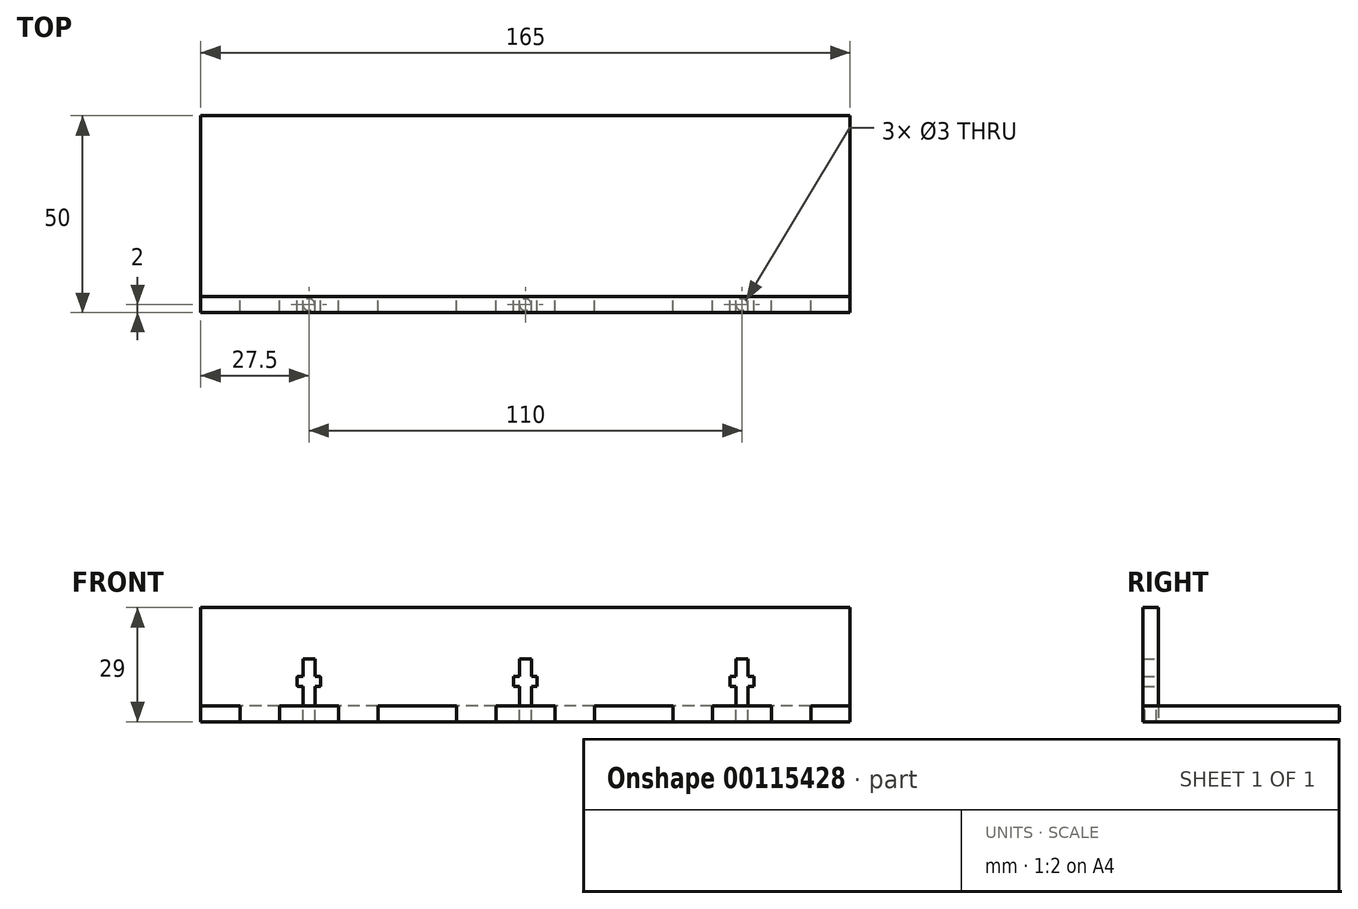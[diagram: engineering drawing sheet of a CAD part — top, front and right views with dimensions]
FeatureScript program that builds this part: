
annotation { "Feature Type Name" : "Feature", "Feature Type Description" : "" }
export const myFeature = defineFeature(function(context is Context, id is Id, definition is map)
    precondition{}
    {
        {
            var Q0;
            Q0=qCreatedBy(makeId("Front.planeOp"),FACE);
            var sketch = newSketch(context, id + "F0", { "sketchPlane" : qUnion([Q0])});
            skLineSegment(sketch, "E0.top", {"start": v(-2.5, 25) * mm, "end": v(162.5, 25) * mm});
            skLineSegment(sketch, "E0.left", {"start": v(-2.5, 0) * mm, "end": v(-2.5, 25) * mm});
            skLineSegment(sketch, "E0.right", {"start": v(162.5, 0) * mm, "end": v(162.5, 25) * mm});
            skLineSegment(sketch, "E1.trimOffspring", {"start": v(-2.5, 0) * mm, "end": v(7.5, 0) * mm});
            skLineSegment(sketch, "E2.top", {"start": v(23.5, 12) * mm, "end": v(26.5, 12) * mm});
            skLineSegment(sketch, "E2.left", {"start": v(23.5, 0) * mm, "end": v(23.5, 5) * mm});
            skLineSegment(sketch, "E2.right", {"start": v(26.5, 0) * mm, "end": v(26.5, 5) * mm});
            skLineSegment(sketch, "E3", {"start": v(25, 12) * mm, "end": v(25, 0) * mm, "construction": true});
            skLineSegment(sketch, "E4.bottom", {"start": v(27.75, 5) * mm, "end": v(26.5, 5) * mm});
            skLineSegment(sketch, "E4.top", {"start": v(27.75, 7.5) * mm, "end": v(26.5, 7.5) * mm});
            skLineSegment(sketch, "E4.left", {"start": v(28, 5.25) * mm, "end": v(28, 7.25) * mm});
            skLineSegment(sketch, "E4.right", {"start": v(22, 5.25) * mm, "end": v(22, 7.25) * mm});
            skPoint(sketch, "E4.middle", {"position": v(25, 6.25) * mm});
            skLineSegment(sketch, "E5.top", {"start": v(32.5, -4) * mm, "end": v(42.5, -4) * mm});
            skLineSegment(sketch, "E5.left", {"start": v(32.5, 0) * mm, "end": v(32.5, -4) * mm});
            skLineSegment(sketch, "E5.right", {"start": v(42.5, 0) * mm, "end": v(42.5, -4) * mm});
            skLineSegment(sketch, "E6.top", {"start": v(7.5, -4) * mm, "end": v(17.5, -4) * mm});
            skLineSegment(sketch, "E6.left", {"start": v(7.5, 0) * mm, "end": v(7.5, -4) * mm});
            skLineSegment(sketch, "E6.right", {"start": v(17.5, 0) * mm, "end": v(17.5, -4) * mm});
            skLineSegment(sketch, "E7.trimOffspring", {"start": v(23.5, 7.5) * mm, "end": v(22.25, 7.5) * mm});
            skLineSegment(sketch, "E8.trimOffspring", {"start": v(26.5, 7.5) * mm, "end": v(26.5, 12) * mm});
            skLineSegment(sketch, "E9.trimOffspring", {"start": v(23.5, 5) * mm, "end": v(22.25, 5) * mm});
            skLineSegment(sketch, "E10.trimOffspring", {"start": v(23.5, 7.5) * mm, "end": v(23.5, 12) * mm});
            skLineSegment(sketch, "E11.trimOffspring", {"start": v(26.5, 0) * mm, "end": v(32.5, 0) * mm});
            skLineSegment(sketch, "E12.trimOffspring", {"start": v(42.5, 0) * mm, "end": v(62.5, 0) * mm});
            skLineSegment(sketch, "E13.trimOffspring", {"start": v(17.5, 0) * mm, "end": v(23.5, 0) * mm});
            skLineSegment(sketch, "E14.1.0.0", {"start": v(78.5, 0) * mm, "end": v(78.5, 5) * mm});
            skPoint(sketch, "E14.1.0.1", {"position": v(80, 6.25) * mm});
            skLineSegment(sketch, "E14.1.0.2", {"start": v(80, 12) * mm, "end": v(80, 0) * mm, "construction": true});
            skLineSegment(sketch, "E14.1.0.3", {"start": v(78.5, 7.5) * mm, "end": v(78.5, 12) * mm});
            skLineSegment(sketch, "E14.1.0.4", {"start": v(81.5, 7.5) * mm, "end": v(81.5, 12) * mm});
            skLineSegment(sketch, "E14.1.0.5", {"start": v(81.5, 0) * mm, "end": v(81.5, 5) * mm});
            skLineSegment(sketch, "E14.1.0.6", {"start": v(78.5, 5) * mm, "end": v(77, 5) * mm});
            skLineSegment(sketch, "E14.1.0.7", {"start": v(78.5, 7.5) * mm, "end": v(77, 7.5) * mm});
            skLineSegment(sketch, "E14.1.0.8", {"start": v(83, 7.5) * mm, "end": v(81.5, 7.5) * mm});
            skLineSegment(sketch, "E14.1.0.9", {"start": v(78.5, 12) * mm, "end": v(81.5, 12) * mm});
            skLineSegment(sketch, "E14.1.0.10", {"start": v(83, 5) * mm, "end": v(81.5, 5) * mm});
            skLineSegment(sketch, "E14.1.0.11", {"start": v(77, 5) * mm, "end": v(77, 7.5) * mm});
            skLineSegment(sketch, "E14.1.0.12", {"start": v(83, 5) * mm, "end": v(83, 7.5) * mm});
            skLineSegment(sketch, "E14.1.0.13", {"start": v(87.5, -4) * mm, "end": v(97.5, -4) * mm});
            skLineSegment(sketch, "E14.1.0.14", {"start": v(62.5, -4) * mm, "end": v(72.5, -4) * mm});
            skLineSegment(sketch, "E14.1.0.15", {"start": v(72.5, 0) * mm, "end": v(72.5, -4) * mm});
            skLineSegment(sketch, "E14.1.0.16", {"start": v(62.5, 0) * mm, "end": v(62.5, -4) * mm});
            skLineSegment(sketch, "E14.1.0.17", {"start": v(87.5, 0) * mm, "end": v(87.5, -4) * mm});
            skLineSegment(sketch, "E14.1.0.18", {"start": v(97.5, 0) * mm, "end": v(97.5, -4) * mm});
            skLineSegment(sketch, "E14.2.0.0", {"start": v(133.5, 0) * mm, "end": v(133.5, 5) * mm});
            skPoint(sketch, "E14.2.0.1", {"position": v(135, 6.25) * mm});
            skLineSegment(sketch, "E14.2.0.2", {"start": v(135, 12) * mm, "end": v(135, 0) * mm, "construction": true});
            skLineSegment(sketch, "E14.2.0.3", {"start": v(133.5, 7.5) * mm, "end": v(133.5, 12) * mm});
            skLineSegment(sketch, "E14.2.0.4", {"start": v(136.5, 7.5) * mm, "end": v(136.5, 12) * mm});
            skLineSegment(sketch, "E14.2.0.5", {"start": v(136.5, 0) * mm, "end": v(136.5, 5) * mm});
            skLineSegment(sketch, "E14.2.0.6", {"start": v(133.5, 5) * mm, "end": v(132, 5) * mm});
            skLineSegment(sketch, "E14.2.0.7", {"start": v(133.5, 7.5) * mm, "end": v(132, 7.5) * mm});
            skLineSegment(sketch, "E14.2.0.8", {"start": v(138, 7.5) * mm, "end": v(136.5, 7.5) * mm});
            skLineSegment(sketch, "E14.2.0.9", {"start": v(133.5, 12) * mm, "end": v(136.5, 12) * mm});
            skLineSegment(sketch, "E14.2.0.10", {"start": v(138, 5) * mm, "end": v(136.5, 5) * mm});
            skLineSegment(sketch, "E14.2.0.11", {"start": v(132, 5) * mm, "end": v(132, 7.5) * mm});
            skLineSegment(sketch, "E14.2.0.12", {"start": v(138, 5) * mm, "end": v(138, 7.5) * mm});
            skLineSegment(sketch, "E14.2.0.13", {"start": v(142.5, -4) * mm, "end": v(152.5, -4) * mm});
            skLineSegment(sketch, "E14.2.0.14", {"start": v(117.5, -4) * mm, "end": v(127.5, -4) * mm});
            skLineSegment(sketch, "E14.2.0.15", {"start": v(127.5, 0) * mm, "end": v(127.5, -4) * mm});
            skLineSegment(sketch, "E14.2.0.16", {"start": v(117.5, 0) * mm, "end": v(117.5, -4) * mm});
            skLineSegment(sketch, "E14.2.0.17", {"start": v(142.5, 0) * mm, "end": v(142.5, -4) * mm});
            skLineSegment(sketch, "E14.2.0.18", {"start": v(152.5, 0) * mm, "end": v(152.5, -4) * mm});
            skLineSegment(sketch, "E14.direction1", {"start": v(7.5, -4) * mm, "end": v(62.5, -4) * mm, "construction": true});
            skLineSegment(sketch, "E15.trimOffspring", {"start": v(152.5, 0) * mm, "end": v(162.5, 0) * mm});
            skLineSegment(sketch, "E16.trimOffspring", {"start": v(136.5, 0) * mm, "end": v(142.5, 0) * mm});
            skLineSegment(sketch, "E17.trimOffspring", {"start": v(127.5, 0) * mm, "end": v(133.5, 0) * mm});
            skLineSegment(sketch, "E18.trimOffspring", {"start": v(97.5, 0) * mm, "end": v(117.5, 0) * mm});
            skLineSegment(sketch, "E19.trimOffspring", {"start": v(81.5, 0) * mm, "end": v(87.5, 0) * mm});
            skLineSegment(sketch, "E20.trimOffspring", {"start": v(72.5, 0) * mm, "end": v(78.5, 0) * mm});
            skPoint(sketch, "E21.visualSharp", {"position": v(28, 5) * mm});
            skArc(sketch, "E21.filletArc", {"start": v(27.75, 5) * mm, "mid": v(27.93, 5.07) * mm, "end": v(28, 5.25) * mm});
            skPoint(sketch, "E22.visualSharp", {"position": v(28, 7.5) * mm});
            skArc(sketch, "E22.filletArc", {"start": v(28, 7.25) * mm, "mid": v(27.93, 7.43) * mm, "end": v(27.75, 7.5) * mm});
            skPoint(sketch, "E23.visualSharp", {"position": v(22, 5) * mm});
            skArc(sketch, "E23.filletArc", {"start": v(22, 5.25) * mm, "mid": v(22.07, 5.07) * mm, "end": v(22.25, 5) * mm});
            skPoint(sketch, "E24.visualSharp", {"position": v(22, 7.5) * mm});
            skArc(sketch, "E24.filletArc", {"start": v(22.25, 7.5) * mm, "mid": v(22.07, 7.43) * mm, "end": v(22, 7.25) * mm});
            skSolve(sketch);
        }
        {
            var Q0;
            Q0=makeQuery(id+"F0.imprint","IMPRINT",FACE,{"disambiguationData":[TD([[makeQuery(id+"F0.imprint","IMPRINT",EDGE,{"derivedFrom":sQuery(id+"F0.wireOp",EDGE,"E0.top")}),-1.0]])]});
            extrude(context, id + "F1", {"entities" : qUnion([Q0]), "depth" : 4 * mm});
        }
        {
            var Q0;
            Q0=makeQuery(id+"F1.opExtrude","SWEPT_FACE",FACE,{"disambiguationData":[OSD([sQuery(id+"F0.wireOp",EDGE,"E12.trimOffspring")])]});
            var sketch = newSketch(context, id + "F2", { "sketchPlane" : qUnion([Q0])});
            skLineSegment(sketch, "E25.bottom", {"start": v(-2.5, 4) * mm, "end": v(162.5, 4) * mm});
            skLineSegment(sketch, "E25.top", {"start": v(-2.5, -46) * mm, "end": v(162.5, -46) * mm});
            skLineSegment(sketch, "E25.left", {"start": v(-2.5, 4) * mm, "end": v(-2.5, -46) * mm});
            skLineSegment(sketch, "E25.right", {"start": v(162.5, 4) * mm, "end": v(162.5, -46) * mm});
            skPoint(sketch, "E26.0", {"position": v(162.5, 4) * mm});
            skPoint(sketch, "E27.0", {"position": v(-2.5, 4) * mm});
            skLineSegment(sketch, "E28.0", {"start": v(23.5, 4) * mm, "end": v(23.5, 0) * mm, "construction": true});
            skLineSegment(sketch, "E29.0", {"start": v(26.5, 4) * mm, "end": v(26.5, 0) * mm, "construction": true});
            skLineSegment(sketch, "E30", {"start": v(23.5, 2) * mm, "end": v(26.5, 2) * mm, "construction": true});
            skCircle(sketch, "E31", {"center": v(25, 2) * mm, "radius": 1.5 * mm});
            skCircle(sketch, "E32.1.0.0", {"center": v(80, 2) * mm, "radius": 1.5 * mm});
            skCircle(sketch, "E32.2.0.0", {"center": v(135, 2) * mm, "radius": 1.5 * mm});
            skLineSegment(sketch, "E32.direction1", {"start": v(25, 2) * mm, "end": v(80, 2) * mm, "construction": true});
            skLineSegment(sketch, "E33.0.0", {"start": v(97.5, 0) * mm, "end": v(117.5, 0) * mm, "construction": true});
            skLineSegment(sketch, "E33.0.1", {"start": v(117.5, 0) * mm, "end": v(117.5, 4) * mm, "construction": true});
            skLineSegment(sketch, "E33.0.2", {"start": v(117.5, 4) * mm, "end": v(97.5, 4) * mm, "construction": true});
            skLineSegment(sketch, "E33.0.3", {"start": v(97.5, 4) * mm, "end": v(97.5, 0) * mm, "construction": true});
            skSolve(sketch);
        }
        {
            var Q0;
            Q0 = qSketchRegion(id + "F2", true);
            extrude(context, id + "F3", {"entities" : qUnion([Q0]), "depth" : 4 * mm});
        }
        {
            var Q0;
            Q0=makeQuery(id+"F1.opExtrude","SWEPT_BODY",BODY,{"disambiguationData":[OSD([sQuery(id+"F0.wireOp",EDGE,"E0.top"),sQuery(id+"F0.wireOp",EDGE,"E0.left"),sQuery(id+"F0.wireOp",EDGE,"E0.right"),sQuery(id+"F0.wireOp",EDGE,"E1.trimOffspring"),sQuery(id+"F0.wireOp",EDGE,"E2.top"),sQuery(id+"F0.wireOp",EDGE,"E2.left"),sQuery(id+"F0.wireOp",EDGE,"E2.right"),sQuery(id+"F0.wireOp",EDGE,"E4.bottom"),sQuery(id+"F0.wireOp",EDGE,"E4.top"),sQuery(id+"F0.wireOp",EDGE,"E4.left"),sQuery(id+"F0.wireOp",EDGE,"E4.right"),sQuery(id+"F0.wireOp",EDGE,"E5.top"),sQuery(id+"F0.wireOp",EDGE,"E5.left"),sQuery(id+"F0.wireOp",EDGE,"E5.right"),sQuery(id+"F0.wireOp",EDGE,"E6.top"),sQuery(id+"F0.wireOp",EDGE,"E6.left"),sQuery(id+"F0.wireOp",EDGE,"E6.right"),sQuery(id+"F0.wireOp",EDGE,"E7.trimOffspring"),sQuery(id+"F0.wireOp",EDGE,"E8.trimOffspring"),sQuery(id+"F0.wireOp",EDGE,"E9.trimOffspring"),sQuery(id+"F0.wireOp",EDGE,"E10.trimOffspring"),sQuery(id+"F0.wireOp",EDGE,"E11.trimOffspring"),sQuery(id+"F0.wireOp",EDGE,"E12.trimOffspring"),sQuery(id+"F0.wireOp",EDGE,"E13.trimOffspring"),sQuery(id+"F0.wireOp",EDGE,"E14.1.0.0"),sQuery(id+"F0.wireOp",EDGE,"E14.1.0.3"),sQuery(id+"F0.wireOp",EDGE,"E14.1.0.4"),sQuery(id+"F0.wireOp",EDGE,"E14.1.0.5"),sQuery(id+"F0.wireOp",EDGE,"E14.1.0.6"),sQuery(id+"F0.wireOp",EDGE,"E14.1.0.7"),sQuery(id+"F0.wireOp",EDGE,"E14.1.0.8"),sQuery(id+"F0.wireOp",EDGE,"E14.1.0.9"),sQuery(id+"F0.wireOp",EDGE,"E14.1.0.10"),sQuery(id+"F0.wireOp",EDGE,"E14.1.0.11"),sQuery(id+"F0.wireOp",EDGE,"E14.1.0.12"),sQuery(id+"F0.wireOp",EDGE,"E14.1.0.13"),sQuery(id+"F0.wireOp",EDGE,"E14.1.0.14"),sQuery(id+"F0.wireOp",EDGE,"E14.1.0.15"),sQuery(id+"F0.wireOp",EDGE,"E14.1.0.16"),sQuery(id+"F0.wireOp",EDGE,"E14.1.0.17"),sQuery(id+"F0.wireOp",EDGE,"E14.1.0.18"),sQuery(id+"F0.wireOp",EDGE,"E14.2.0.0"),sQuery(id+"F0.wireOp",EDGE,"E14.2.0.3"),sQuery(id+"F0.wireOp",EDGE,"E14.2.0.4"),sQuery(id+"F0.wireOp",EDGE,"E14.2.0.5"),sQuery(id+"F0.wireOp",EDGE,"E14.2.0.6"),sQuery(id+"F0.wireOp",EDGE,"E14.2.0.7"),sQuery(id+"F0.wireOp",EDGE,"E14.2.0.8"),sQuery(id+"F0.wireOp",EDGE,"E14.2.0.9"),sQuery(id+"F0.wireOp",EDGE,"E14.2.0.10"),sQuery(id+"F0.wireOp",EDGE,"E14.2.0.11"),sQuery(id+"F0.wireOp",EDGE,"E14.2.0.12"),sQuery(id+"F0.wireOp",EDGE,"E14.2.0.13"),sQuery(id+"F0.wireOp",EDGE,"E14.2.0.14"),sQuery(id+"F0.wireOp",EDGE,"E14.2.0.15"),sQuery(id+"F0.wireOp",EDGE,"E14.2.0.16"),sQuery(id+"F0.wireOp",EDGE,"E14.2.0.17"),sQuery(id+"F0.wireOp",EDGE,"E14.2.0.18"),sQuery(id+"F0.wireOp",EDGE,"E15.trimOffspring"),sQuery(id+"F0.wireOp",EDGE,"E16.trimOffspring"),sQuery(id+"F0.wireOp",EDGE,"E17.trimOffspring"),sQuery(id+"F0.wireOp",EDGE,"E18.trimOffspring"),sQuery(id+"F0.wireOp",EDGE,"E19.trimOffspring"),sQuery(id+"F0.wireOp",EDGE,"E20.trimOffspring"),sQuery(id+"F0.wireOp",EDGE,"E21.filletArc"),sQuery(id+"F0.wireOp",EDGE,"E22.filletArc"),sQuery(id+"F0.wireOp",EDGE,"E23.filletArc"),sQuery(id+"F0.wireOp",EDGE,"E24.filletArc")])]});
            var Q1;
            Q1=makeQuery(id+"F3.opExtrude","SWEPT_BODY",BODY,{"disambiguationData":[OSD([sQuery(id+"F2.wireOp",EDGE,"E25.bottom"),sQuery(id+"F2.wireOp",EDGE,"E25.top"),sQuery(id+"F2.wireOp",EDGE,"E25.left"),sQuery(id+"F2.wireOp",EDGE,"E25.right"),sQuery(id+"F2.wireOp",EDGE,"E31"),sQuery(id+"F2.wireOp",EDGE,"E32.1.0.0"),sQuery(id+"F2.wireOp",EDGE,"E32.2.0.0")])]});
            booleanBodies(context, id + "F4", {"operationType" : BooleanOperationType.SUBTRACTION, "tools" : qUnion([Q0]), "targets" : qUnion([Q1]), "keepTools" : true});
        }
    });
